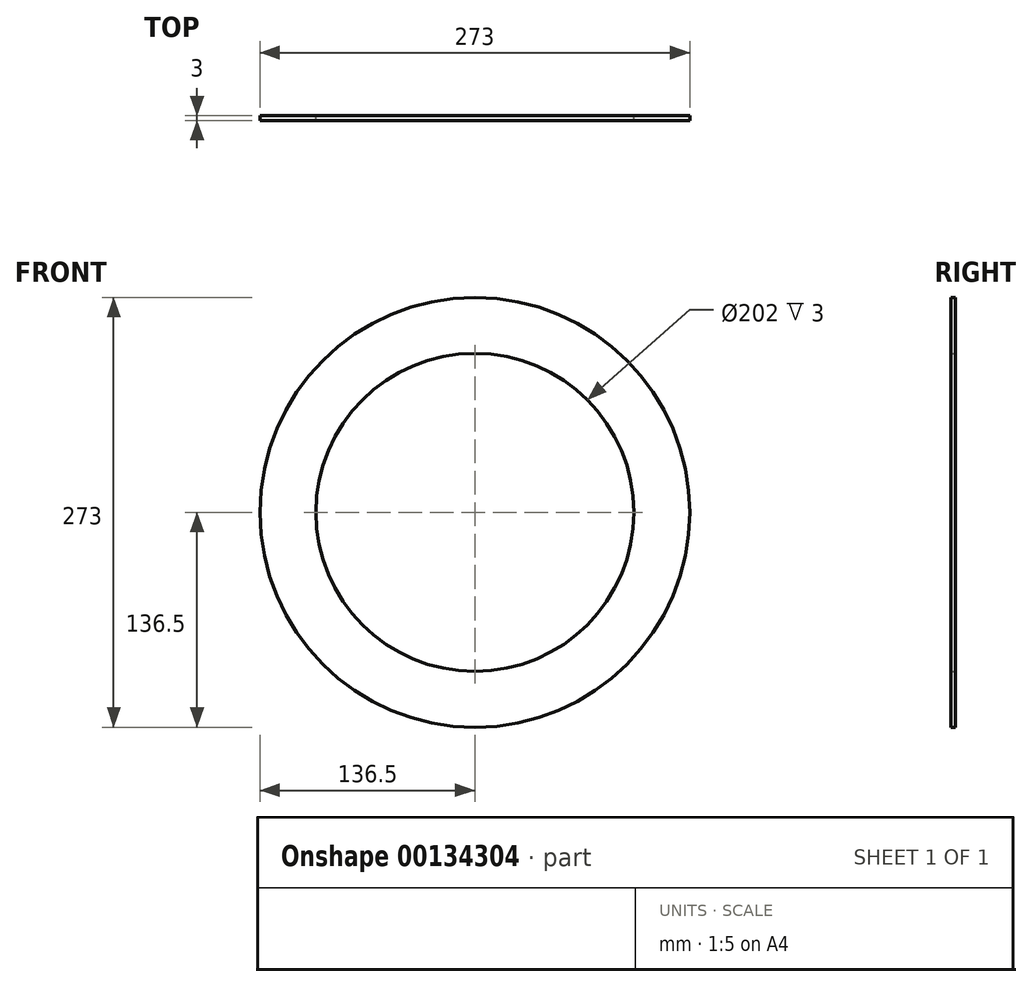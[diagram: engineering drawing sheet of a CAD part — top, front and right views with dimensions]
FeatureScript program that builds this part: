
annotation { "Feature Type Name" : "Feature", "Feature Type Description" : "" }
export const myFeature = defineFeature(function(context is Context, id is Id, definition is map)
    precondition{}
    {
        {
            var Q0;
            Q0=qCreatedBy(makeId("Front.planeOp"),FACE);
            var sketch = newSketch(context, id + "F0", { "sketchPlane" : qUnion([Q0])});
            skCircle(sketch, "E0", {"center": v(0, 0) * mm, "radius": 101 * mm});
            skCircle(sketch, "E1", {"center": v(0, 0) * mm, "radius": 136.5 * mm});
            skSolve(sketch);
        }
        {
            var Q0;
            Q0=makeQuery(id+"F0.imprint","IMPRINT",FACE,{"disambiguationData":[TD([[makeQuery(id+"F0.imprint","IMPRINT",EDGE,{"derivedFrom":sQuery(id+"F0.wireOp",EDGE,"E0")}),-1.0]])]});
            extrude(context, id + "F1", {"entities" : qUnion([Q0]), "depth" : 3 * mm});
        }
    });
